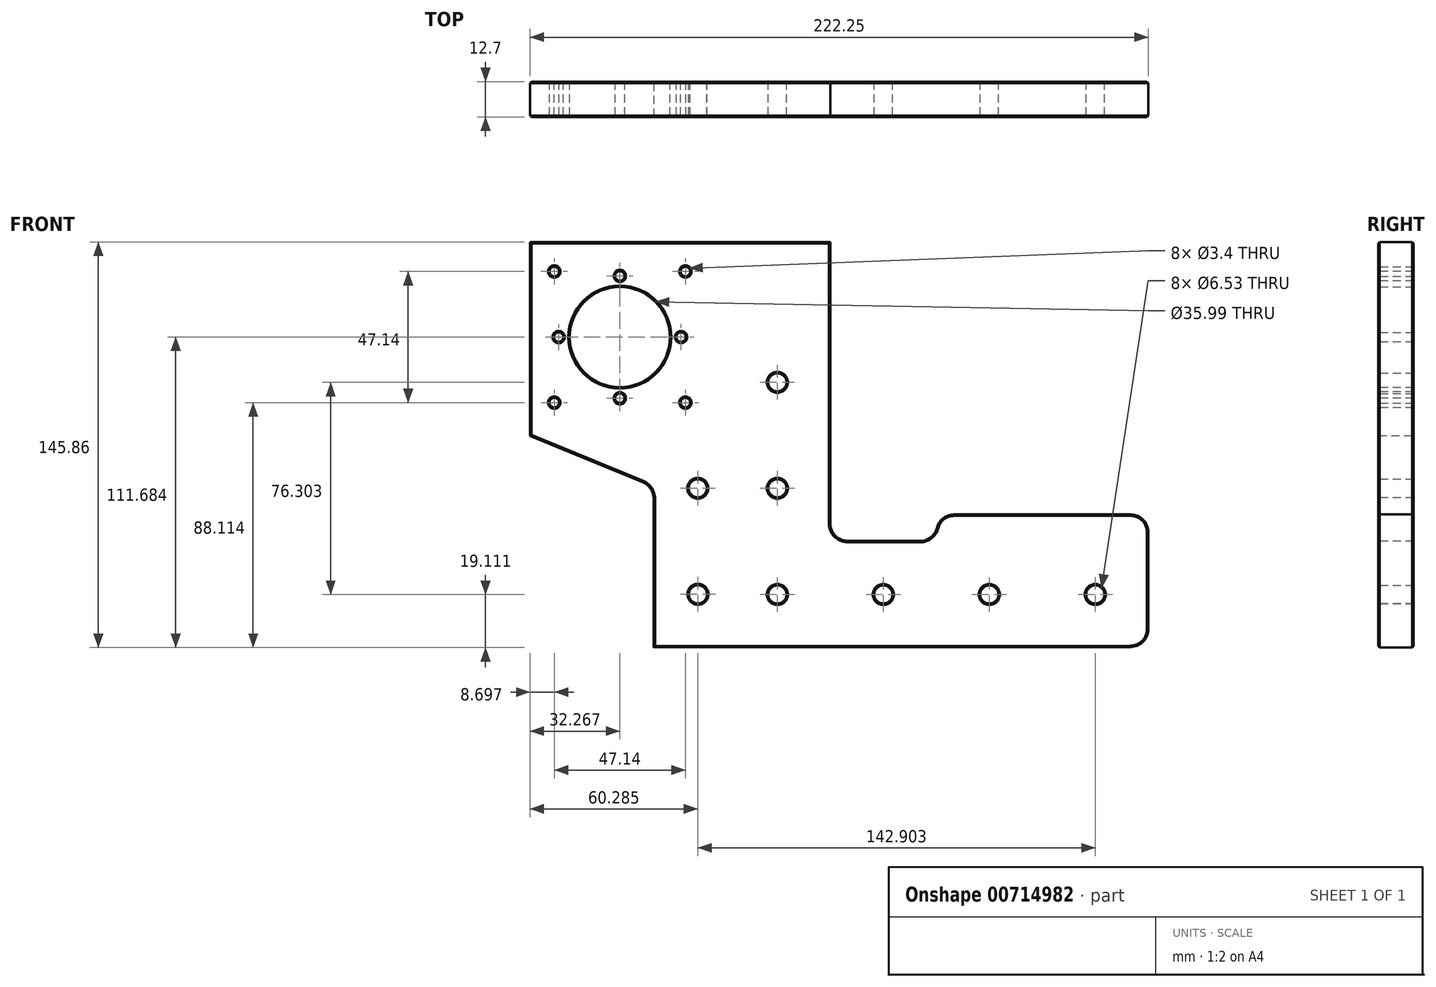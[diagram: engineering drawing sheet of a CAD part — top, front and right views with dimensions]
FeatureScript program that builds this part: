
annotation { "Feature Type Name" : "Feature", "Feature Type Description" : "" }
export const myFeature = defineFeature(function(context is Context, id is Id, definition is map)
    precondition{}
    {
        {
            var Q0;
            Q0=qCreatedBy(makeId("Front.planeOp"),FACE);
            var sketch = newSketch(context, id + "F0", { "sketchPlane" : qUnion([Q0])});
            skLineSegment(sketch, "E0.bottom", {"start": v(95.58, -98.53) * mm, "end": v(-126.67, -98.85) * mm});
            skLineSegment(sketch, "E1", {"start": v(-18.72, 66.25) * mm, "end": v(-18.72, -60.43) * mm});
            skLineSegment(sketch, "E2", {"start": v(95.58, -60.43) * mm, "end": v(95.58, -98.53) * mm});
            skLineSegment(sketch, "E3", {"start": v(-126.67, -98.85) * mm, "end": v(-126.67, 66.25) * mm});
            skLineSegment(sketch, "E4", {"start": v(-126.67, 66.25) * mm, "end": v(-18.72, 66.25) * mm});
            skCircle(sketch, "E5", {"center": v(-37.78, -3.37) * mm, "radius": 3.26 * mm});
            skCircle(sketch, "E6", {"center": v(-37.78, -41.47) * mm, "radius": 3.26 * mm});
            skCircle(sketch, "E7", {"center": v(-37.78, -79.67) * mm, "radius": 3.26 * mm});
            skCircle(sketch, "E8", {"center": v(0.32, -79.67) * mm, "radius": 3.26 * mm});
            skCircle(sketch, "E9", {"center": v(38.42, -79.67) * mm, "radius": 3.26 * mm});
            skCircle(sketch, "E10", {"center": v(76.52, -79.67) * mm, "radius": 3.26 * mm});
            skLineSegment(sketch, "E11", {"start": v(-18.72, -60.43) * mm, "end": v(19.38, -60.43) * mm});
            skLineSegment(sketch, "E12", {"start": v(95.58, -60.43) * mm, "end": v(95.58, -60.43) * mm});
            skLineSegment(sketch, "E13", {"start": v(19.38, -60.43) * mm, "end": v(19.38, -50.9) * mm});
            skLineSegment(sketch, "E14", {"start": v(19.38, -50.9) * mm, "end": v(95.58, -50.9) * mm});
            skLineSegment(sketch, "E15", {"start": v(95.58, -50.9) * mm, "end": v(95.58, -60.43) * mm});
            skCircle(sketch, "E16", {"center": v(-94.4, 12.9) * mm, "radius": 18 * mm});
            skLineSegment(sketch, "E17", {"start": v(-94.4, -17.86) * mm, "end": v(-94.4, 47.16) * mm, "construction": true});
            skLineSegment(sketch, "E18", {"start": v(-126.67, 12.9) * mm, "end": v(-62, 12.9) * mm, "construction": true});
            skLineSegment(sketch, "E19", {"start": v(-121.14, 39.64) * mm, "end": v(-64.04, -17.46) * mm, "construction": true});
            skLineSegment(sketch, "E20", {"start": v(-125.8, -18.5) * mm, "end": v(-61.56, 45.74) * mm, "construction": true});
            skCircle(sketch, "E21", {"center": v(-117.97, 36.47) * mm, "radius": 1.7 * mm});
            skCircle(sketch, "E22.MirrorC", {"center": v(-70.83, 36.47) * mm, "radius": 1.7 * mm});
            skCircle(sketch, "E23.MirrorC", {"center": v(-117.97, -10.67) * mm, "radius": 1.7 * mm});
            skCircle(sketch, "E24.MirrorC", {"center": v(-70.83, -10.67) * mm, "radius": 1.7 * mm});
            skCircle(sketch, "E25", {"center": v(-66.39, -41.47) * mm, "radius": 3.26 * mm});
            skCircle(sketch, "E26", {"center": v(-66.33, -79.6) * mm, "radius": 3.26 * mm});
            skCircle(sketch, "E27", {"center": v(-94.4, 34.9) * mm, "radius": 1.7 * mm});
            skCircle(sketch, "E28", {"center": v(-94.4, -9.1) * mm, "radius": 1.7 * mm});
            skCircle(sketch, "E29", {"center": v(-116.4, 12.9) * mm, "radius": 1.7 * mm});
            skCircle(sketch, "E30", {"center": v(-72.4, 12.9) * mm, "radius": 1.7 * mm});
            skSolve(sketch);
        }
        {
            var Q0;
            Q0=makeQuery(id+"F0.imprint","IMPRINT",FACE,{"disambiguationData":[TD([[makeQuery(id+"F0.imprint","IMPRINT",EDGE,{"derivedFrom":sQuery(id+"F0.wireOp",EDGE,"E0.bottom")}),-1.0]])]});
            var Q1;
            Q1=makeQuery(id+"F0.imprint","IMPRINT",FACE,{"disambiguationData":[TD([[makeQuery(id+"F0.imprint","IMPRINT",EDGE,{"derivedFrom":sQuery(id+"F0.wireOp",EDGE,"f8804403-6028-4e43-9a19-03b2f7b60726.bottom")}),1.0]])]});
            extrude(context, id + "F1", {"entities" : qUnion([Q0, Q1]), "depth" : 12.7 * mm, "offsetDistance" : 25.4 * mm});
        }
        {
            var Q0;
            Q0=makeQuery(id+"F1.opExtrude","CAP_FACE",FACE,{"disambiguationData":[OSD([sQuery(id+"F0.wireOp",EDGE,"E0.bottom"),sQuery(id+"F0.wireOp",EDGE,"E1"),sQuery(id+"F0.wireOp",EDGE,"E2"),sQuery(id+"F0.wireOp",EDGE,"E3"),sQuery(id+"F0.wireOp",EDGE,"E4"),sQuery(id+"F0.wireOp",EDGE,"E5"),sQuery(id+"F0.wireOp",EDGE,"E6"),sQuery(id+"F0.wireOp",EDGE,"E7"),sQuery(id+"F0.wireOp",EDGE,"E8"),sQuery(id+"F0.wireOp",EDGE,"E9"),sQuery(id+"F0.wireOp",EDGE,"E10"),sQuery(id+"F0.wireOp",EDGE,"E11"),sQuery(id+"F0.wireOp",EDGE,"E13"),sQuery(id+"F0.wireOp",EDGE,"E14"),sQuery(id+"F0.wireOp",EDGE,"E15"),sQuery(id+"F0.wireOp",EDGE,"bdd12513-527b-488f-8d6b-20c45a8fa37b"),sQuery(id+"F0.wireOp",EDGE,"499d763e-db54-49f2-b91b-3f217bddd69d"),sQuery(id+"F0.wireOp",EDGE,"cc43b1b5-cebb-45d5-b199-afc85f6befad"),sQuery(id+"F0.wireOp",EDGE,"b27666f3-d0bd-404c-b8eb-62ebadabed05"),sQuery(id+"F0.wireOp",EDGE,"E16")])],"isStart":false});
            var sketch = newSketch(context, id + "F2", { "sketchPlane" : qUnion([Q0])});
            skLineSegment(sketch, "E31", {"start": v(-126.67, 47.08) * mm, "end": v(-18.72, 47.08) * mm});
            skLineSegment(sketch, "E32", {"start": v(-126.67, -22.66) * mm, "end": v(-82.26, -40.92) * mm});
            skLineSegment(sketch, "E33", {"start": v(-82.26, -40.92) * mm, "end": v(-82.26, -98.85) * mm});
            skSolve(sketch);
        }
        {
            var Q0;
            {var subQ0=sQuery(id+"F2.wireOp",EDGE,"E32");Q0=makeQuery(id+"F2.imprint","IMPRINT",FACE,{"disambiguationData":[TD([[makeQuery(id+"F2.imprint","IMPRINT",EDGE,{"derivedFrom":subQ0}),-1.0]])]});}
            var Q1;
            {var subQ0=sQuery(id+"F2.wireOp",EDGE,"E31");Q1=makeQuery(id+"F2.imprint","IMPRINT",FACE,{"disambiguationData":[TD([[makeQuery(id+"F2.imprint","IMPRINT",EDGE,{"derivedFrom":subQ0}),1.0]])]});}
            extrude(context, id + "F3", {"entities" : qUnion([Q0, Q1]), "operationType" : NewBodyOperationType.REMOVE, "oppositeDirection" : true, "depth" : 25.4 * mm, "offsetDistance" : 25.4 * mm});
        }
        {
            var Q0;
            Q0=makeQuery(id+"F3.boolean.opBoolean","COPY",EDGE,{"derivedFrom":makeQuery(id+"F3.opExtrude","SWEPT_EDGE",EDGE,{"disambiguationData":[OSD([sQuery(id+"F0.wireOp",EDGE,"E3"),sQuery(id+"F2.wireOp",EDGE,"E31")])]})});
            var Q1;
            Q1=makeQuery(id+"F3.boolean.opBoolean","COPY",EDGE,{"derivedFrom":makeQuery(id+"F3.opExtrude","SWEPT_EDGE",EDGE,{"disambiguationData":[OSD([sQuery(id+"F0.wireOp",EDGE,"E3"),sQuery(id+"F2.wireOp",EDGE,"E32")])]})});
            var Q2;
            Q2=makeQuery(id+"F3.boolean.opBoolean","COPY",EDGE,{"derivedFrom":makeQuery(id+"F3.opExtrude","SWEPT_EDGE",EDGE,{"disambiguationData":[OSD([sQuery(id+"F0.wireOp",EDGE,"E1"),sQuery(id+"F2.wireOp",EDGE,"E31")])]})});
            var Q3;
            Q3=makeQuery(id+"F3.boolean.opBoolean","COPY",EDGE,{"derivedFrom":makeQuery(id+"F3.opExtrude","SWEPT_EDGE",EDGE,{"disambiguationData":[OSD([sQuery(id+"F2.wireOp",EDGE,"E32"),sQuery(id+"F2.wireOp",EDGE,"E33")])]})});
            var Q4;
            Q4=makeQuery(id+"F3.boolean.opBoolean","COPY",EDGE,{"derivedFrom":makeQuery(id+"F3.opExtrude","SWEPT_EDGE",EDGE,{"disambiguationData":[OSD([sQuery(id+"F0.wireOp",EDGE,"E0.bottom"),sQuery(id+"F2.wireOp",EDGE,"E33")])]})});
            var Q5;
            Q5=makeQuery(id+"F1.opExtrude","SWEPT_EDGE",EDGE,{"disambiguationData":[OSD([sQuery(id+"F0.wireOp",EDGE,"E0.bottom"),sQuery(id+"F0.wireOp",EDGE,"E2")])]});
            var Q6;
            Q6=makeQuery(id+"F1.opExtrude","SWEPT_EDGE",EDGE,{"disambiguationData":[OSD([sQuery(id+"F0.wireOp",EDGE,"E14"),sQuery(id+"F0.wireOp",EDGE,"E15")])]});
            var Q7;
            Q7=makeQuery(id+"F1.opExtrude","SWEPT_EDGE",EDGE,{"disambiguationData":[OSD([sQuery(id+"F0.wireOp",EDGE,"E13"),sQuery(id+"F0.wireOp",EDGE,"E14")])]});
            var Q8;
            Q8=makeQuery(id+"F1.opExtrude","SWEPT_EDGE",EDGE,{"disambiguationData":[OSD([sQuery(id+"F0.wireOp",EDGE,"E1"),sQuery(id+"F0.wireOp",EDGE,"E11")])]});
            fillet(context, id + "F4", {"entities" : qUnion([Q0, Q1, Q2, Q3, Q4, Q5, Q6, Q7, Q8]), "radius" : 6.35 * mm, "tangentPropagation" : true, "allowEdgeOverflow" : false});
        }
        {
            var Q0;
            Q0=makeQuery(id+"F1.opExtrude","SWEPT_EDGE",EDGE,{"disambiguationData":[OSD([sQuery(id+"F0.wireOp",EDGE,"E11"),sQuery(id+"F0.wireOp",EDGE,"E13")])]});
            fillet(context, id + "F5", {"entities" : qUnion([Q0]), "radius" : 6.35 * mm, "tangentPropagation" : true, "allowEdgeOverflow" : false});
        }
        {
            var Q0;
            Q0=makeQuery(id+"F1.opExtrude","CAP_FACE",FACE,{"disambiguationData":[OSD([sQuery(id+"F0.wireOp",EDGE,"E0.bottom"),sQuery(id+"F0.wireOp",EDGE,"E1"),sQuery(id+"F0.wireOp",EDGE,"E2"),sQuery(id+"F0.wireOp",EDGE,"E3"),sQuery(id+"F0.wireOp",EDGE,"E4"),sQuery(id+"F0.wireOp",EDGE,"E5"),sQuery(id+"F0.wireOp",EDGE,"E6"),sQuery(id+"F0.wireOp",EDGE,"E7"),sQuery(id+"F0.wireOp",EDGE,"E8"),sQuery(id+"F0.wireOp",EDGE,"E9"),sQuery(id+"F0.wireOp",EDGE,"E10"),sQuery(id+"F0.wireOp",EDGE,"E11"),sQuery(id+"F0.wireOp",EDGE,"E13"),sQuery(id+"F0.wireOp",EDGE,"E14"),sQuery(id+"F0.wireOp",EDGE,"E15"),sQuery(id+"F0.wireOp",EDGE,"E16"),sQuery(id+"F0.wireOp",EDGE,"E21"),sQuery(id+"F0.wireOp",EDGE,"E22.MirrorC"),sQuery(id+"F0.wireOp",EDGE,"E23.MirrorC"),sQuery(id+"F0.wireOp",EDGE,"E24.MirrorC"),sQuery(id+"F0.wireOp",EDGE,"E25"),sQuery(id+"F0.wireOp",EDGE,"E26"),sQuery(id+"F0.wireOp",EDGE,"E27"),sQuery(id+"F0.wireOp",EDGE,"E28"),sQuery(id+"F0.wireOp",EDGE,"E29"),sQuery(id+"F0.wireOp",EDGE,"E30")])],"isStart":false});
            var Q1;
            Q1=makeQuery(id+"F1.opExtrude","CAP_FACE",FACE,{"disambiguationData":[OSD([sQuery(id+"F0.wireOp",EDGE,"E0.bottom"),sQuery(id+"F0.wireOp",EDGE,"E1"),sQuery(id+"F0.wireOp",EDGE,"E2"),sQuery(id+"F0.wireOp",EDGE,"E3"),sQuery(id+"F0.wireOp",EDGE,"E4"),sQuery(id+"F0.wireOp",EDGE,"E5"),sQuery(id+"F0.wireOp",EDGE,"E6"),sQuery(id+"F0.wireOp",EDGE,"E7"),sQuery(id+"F0.wireOp",EDGE,"E8"),sQuery(id+"F0.wireOp",EDGE,"E9"),sQuery(id+"F0.wireOp",EDGE,"E10"),sQuery(id+"F0.wireOp",EDGE,"E11"),sQuery(id+"F0.wireOp",EDGE,"E13"),sQuery(id+"F0.wireOp",EDGE,"E14"),sQuery(id+"F0.wireOp",EDGE,"E15"),sQuery(id+"F0.wireOp",EDGE,"E16"),sQuery(id+"F0.wireOp",EDGE,"E21"),sQuery(id+"F0.wireOp",EDGE,"E22.MirrorC"),sQuery(id+"F0.wireOp",EDGE,"E23.MirrorC"),sQuery(id+"F0.wireOp",EDGE,"E24.MirrorC"),sQuery(id+"F0.wireOp",EDGE,"E25"),sQuery(id+"F0.wireOp",EDGE,"E26"),sQuery(id+"F0.wireOp",EDGE,"E27"),sQuery(id+"F0.wireOp",EDGE,"E28"),sQuery(id+"F0.wireOp",EDGE,"E29"),sQuery(id+"F0.wireOp",EDGE,"E30")])],"isStart":true});
            var Q2;
            {var subQ0=sQuery(id+"F0.wireOp",EDGE,"E24.MirrorC");var subQ1=sQuery(id+"F0.wireOp",EDGE,"E23.MirrorC");var subQ2=sQuery(id+"F0.wireOp",EDGE,"E22.MirrorC");var subQ3=sQuery(id+"F0.wireOp",EDGE,"E21");Q2=makeQuery(id+"FnEefVxFa0R0ueH_1.boolean.opBoolean","MERGE",FACE,{"derivedFrom":[makeQuery(id+"FFe5l9Ppjfo7W1Y_1.opPattern","COPY",FACE,{"derivedFrom":makeQuery(id+"F1.opExtrude","CAP_FACE",FACE,{"disambiguationData":[OSD([sQuery(id+"F0.wireOp",EDGE,"E0.bottom"),sQuery(id+"F0.wireOp",EDGE,"E1"),sQuery(id+"F0.wireOp",EDGE,"E2"),sQuery(id+"F0.wireOp",EDGE,"E3"),sQuery(id+"F0.wireOp",EDGE,"E4"),sQuery(id+"F0.wireOp",EDGE,"E5"),sQuery(id+"F0.wireOp",EDGE,"E6"),sQuery(id+"F0.wireOp",EDGE,"E7"),sQuery(id+"F0.wireOp",EDGE,"E8"),sQuery(id+"F0.wireOp",EDGE,"E9"),sQuery(id+"F0.wireOp",EDGE,"E10"),sQuery(id+"F0.wireOp",EDGE,"E11"),sQuery(id+"F0.wireOp",EDGE,"E13"),sQuery(id+"F0.wireOp",EDGE,"E14"),sQuery(id+"F0.wireOp",EDGE,"E15"),sQuery(id+"F0.wireOp",EDGE,"E16"),subQ3,subQ2,subQ1,subQ0,sQuery(id+"F0.wireOp",EDGE,"E25"),sQuery(id+"F0.wireOp",EDGE,"E26"),sQuery(id+"F0.wireOp",EDGE,"E27"),sQuery(id+"F0.wireOp",EDGE,"E28"),sQuery(id+"F0.wireOp",EDGE,"E29"),sQuery(id+"F0.wireOp",EDGE,"E30")])],"isStart":false}),"instanceName":"1"}),makeQuery(id+"FnEefVxFa0R0ueH_1.opExtrude","CAP_FACE",FACE,{"disambiguationData":[OSD([subQ3])],"isStart":true}),makeQuery(id+"FnEefVxFa0R0ueH_1.opExtrude","CAP_FACE",FACE,{"disambiguationData":[OSD([subQ2])],"isStart":true}),makeQuery(id+"FnEefVxFa0R0ueH_1.opExtrude","CAP_FACE",FACE,{"disambiguationData":[OSD([subQ1])],"isStart":true}),makeQuery(id+"FnEefVxFa0R0ueH_1.opExtrude","CAP_FACE",FACE,{"disambiguationData":[OSD([subQ0])],"isStart":true})]});}
            var Q3;
            {var subQ0=sQuery(id+"F0.wireOp",EDGE,"E24.MirrorC");var subQ1=sQuery(id+"F0.wireOp",EDGE,"E23.MirrorC");var subQ2=sQuery(id+"F0.wireOp",EDGE,"E22.MirrorC");var subQ3=sQuery(id+"F0.wireOp",EDGE,"E21");Q3=makeQuery(id+"FnEefVxFa0R0ueH_1.boolean.opBoolean","MERGE",FACE,{"derivedFrom":[makeQuery(id+"FFe5l9Ppjfo7W1Y_1.opPattern","COPY",FACE,{"derivedFrom":makeQuery(id+"F1.opExtrude","CAP_FACE",FACE,{"disambiguationData":[OSD([sQuery(id+"F0.wireOp",EDGE,"E0.bottom"),sQuery(id+"F0.wireOp",EDGE,"E1"),sQuery(id+"F0.wireOp",EDGE,"E2"),sQuery(id+"F0.wireOp",EDGE,"E3"),sQuery(id+"F0.wireOp",EDGE,"E4"),sQuery(id+"F0.wireOp",EDGE,"E5"),sQuery(id+"F0.wireOp",EDGE,"E6"),sQuery(id+"F0.wireOp",EDGE,"E7"),sQuery(id+"F0.wireOp",EDGE,"E8"),sQuery(id+"F0.wireOp",EDGE,"E9"),sQuery(id+"F0.wireOp",EDGE,"E10"),sQuery(id+"F0.wireOp",EDGE,"E11"),sQuery(id+"F0.wireOp",EDGE,"E13"),sQuery(id+"F0.wireOp",EDGE,"E14"),sQuery(id+"F0.wireOp",EDGE,"E15"),sQuery(id+"F0.wireOp",EDGE,"E16"),subQ3,subQ2,subQ1,subQ0,sQuery(id+"F0.wireOp",EDGE,"E25"),sQuery(id+"F0.wireOp",EDGE,"E26"),sQuery(id+"F0.wireOp",EDGE,"E27"),sQuery(id+"F0.wireOp",EDGE,"E28"),sQuery(id+"F0.wireOp",EDGE,"E29"),sQuery(id+"F0.wireOp",EDGE,"E30")])],"isStart":true}),"instanceName":"1"}),makeQuery(id+"FnEefVxFa0R0ueH_1.opExtrude","CAP_FACE",FACE,{"disambiguationData":[OSD([subQ3])],"isStart":false}),makeQuery(id+"FnEefVxFa0R0ueH_1.opExtrude","CAP_FACE",FACE,{"disambiguationData":[OSD([subQ2])],"isStart":false}),makeQuery(id+"FnEefVxFa0R0ueH_1.opExtrude","CAP_FACE",FACE,{"disambiguationData":[OSD([subQ1])],"isStart":false}),makeQuery(id+"FnEefVxFa0R0ueH_1.opExtrude","CAP_FACE",FACE,{"disambiguationData":[OSD([subQ0])],"isStart":false})]});}
            chamfer(context, id + "F6", {"entities" : qUnion([Q0, Q1, Q2, Q3]), "width" : 0.5 * mm, "tangentPropagation" : true});
        }
    });
